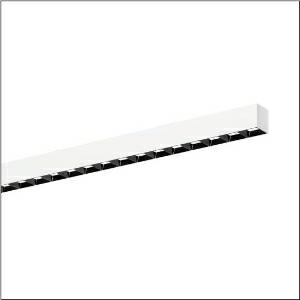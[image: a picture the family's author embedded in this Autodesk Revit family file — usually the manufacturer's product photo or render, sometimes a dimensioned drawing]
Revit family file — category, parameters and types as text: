
# Revit family: silica_r__21_51mx21da34wb_4769
name_source: partatom
category: Lighting Fixtures
units: mm (PartAtom-declared; Revit-internal decimal feet)

## family parameters
Cut with Voids When Loaded = No
Host = Face
Light Source = No
Part Type = Normal
Room Calculation Point = No
Round Connector Dimension = Use Diameter
Shared = No

## types (1)
- --- (1 x LED, 4320 lm, 27.4 W, 3000K)
    Apparent Load = 27 VA
    CIE Flux Codes = 87 99 100 100 100
    Color Rendering = 80
    Color Temperature = 3000K
    Default Elevation = 1800 mm
    Description = Silica® 21, office luminaire, primary light control with darklight reflector, of PMMA, black, CAT 2 (L<= 3000cd/m²), light emission: direct distribution, primary light characteristic: symmetric, installation type: surface-mounted, LED, rated luminous flux: 4.320lm, luminous efficacy: 158lm/W, light colour: 830, colour temperature: 3000K, control gear: DALI 2, with terminal, 3+2-pole, max. 2.5mm², mains connection: 220..240V, AC, 50/60Hz, rated input power: 27.4W, luminaire housing, of aluminium, traffic white (RAL 9016), length: 1.204mm, width: 53mm, height: 53mm, protection rating (complete): IP20, insulation class (complete): insulation class I (protective earthing), certification: CE, permissible operating ambient temperature: 0..+35°C, standard: EN 50419, packaging unit: 1 piece
    Height = 53 mm
    Lamp = 1 x LED
    Lamp Light Flux = 4320 lm
    Lamp Power = 27.4 W
    Lamp count = 1
    Length = 1204 mm
    Luminous efficacy = 158 lm/W
    Manufacturer = Siteco
    ModVariant = No
    Model = 51MX21DA34WB
    Mounting Place = Ceiling
    Mounting Type = Surface mounted
    Number of Poles = 1
    OnlyDefault = Yes
    Power Factor = 1
    Product Name = Silica® 21
    Product group = office luminaire | ceiling mounted
    ProductGroupID = 302
    Protection Class = Protection class I
    Protection Degree = IP 20
    RLX_Detail_Level = 1
    RLX_Emergency_Light_Flux = 0 lm
    RLX_Emergency_Type = 0
    RLX_Emergency_Type_DB = No
    RlxData = <blob elided: 41289 chars, md5=cacd2bf6>
    Socket = socket
    Standby Power = 0 W
    System Light Flux = 4320 lm
    System Power = 27 W
    Type Comments = factory setting: luminous flux: 100 % | dim-lin: 254 | 393 mA
    Type Image = l_1335873.jpg
    URL = http://relux.com
    VarID = @adj_008331
    Voltage = 0 V
    Weight = 0.00 kg
    Width = 53 mm

## geometry (parser evidence)
native form markers: Blend x4, Sweep x11
no freeform markers — native parametric forms only
